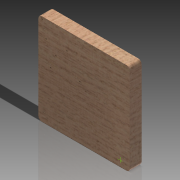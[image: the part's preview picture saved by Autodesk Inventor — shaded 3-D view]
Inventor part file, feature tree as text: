
AUTODESK INVENTOR PART (.ipt)
format: ipt  version: 2014 SP1 (Build 180222100, 222)  size: 146,944 bytes
history: native  units: mm
features: sketch x3, extrude x1, hole x1, fillet x1
ambient origin geometry x8: Origin, YZ Plane, XZ Plane, XY Plane, X Axis, Y Axis, Z Axis, Center Point
bodies: Volumenkörper1 (feature_tree)
feature tree (6):
  extrude  "Extrusion1"  Depth=140.0mm
  hole  "Bohrung1"  [1 undecoded]
  fillet  "Rundung1"  Radius=15.0mm
  sketch  "Skizze1"  dims[d0=140.0mm d1=140.0mm]
  sketch  "Skizze2"  dims[d2=18.0mm d3=0.0mm d4=15.0mm d5=15.0mm]
  sketch  "Skizze3"  dims[d6=15.0mm d7=15.0mm d8=9.0mm d9=9.0mm d10=9.0mm d11=9.0mm d12=2.0mm d13=6.0mm d14=5.0mm d15=2.0mm d16=90.0deg d17=8.0mm d18=20.594885mm d19=5.0mm]
note: 1 required parameter value undecoded (feature->parameter linkage not recoverable at this tier; creation-order binding heuristic only, values carry confidence <= 0.55)
